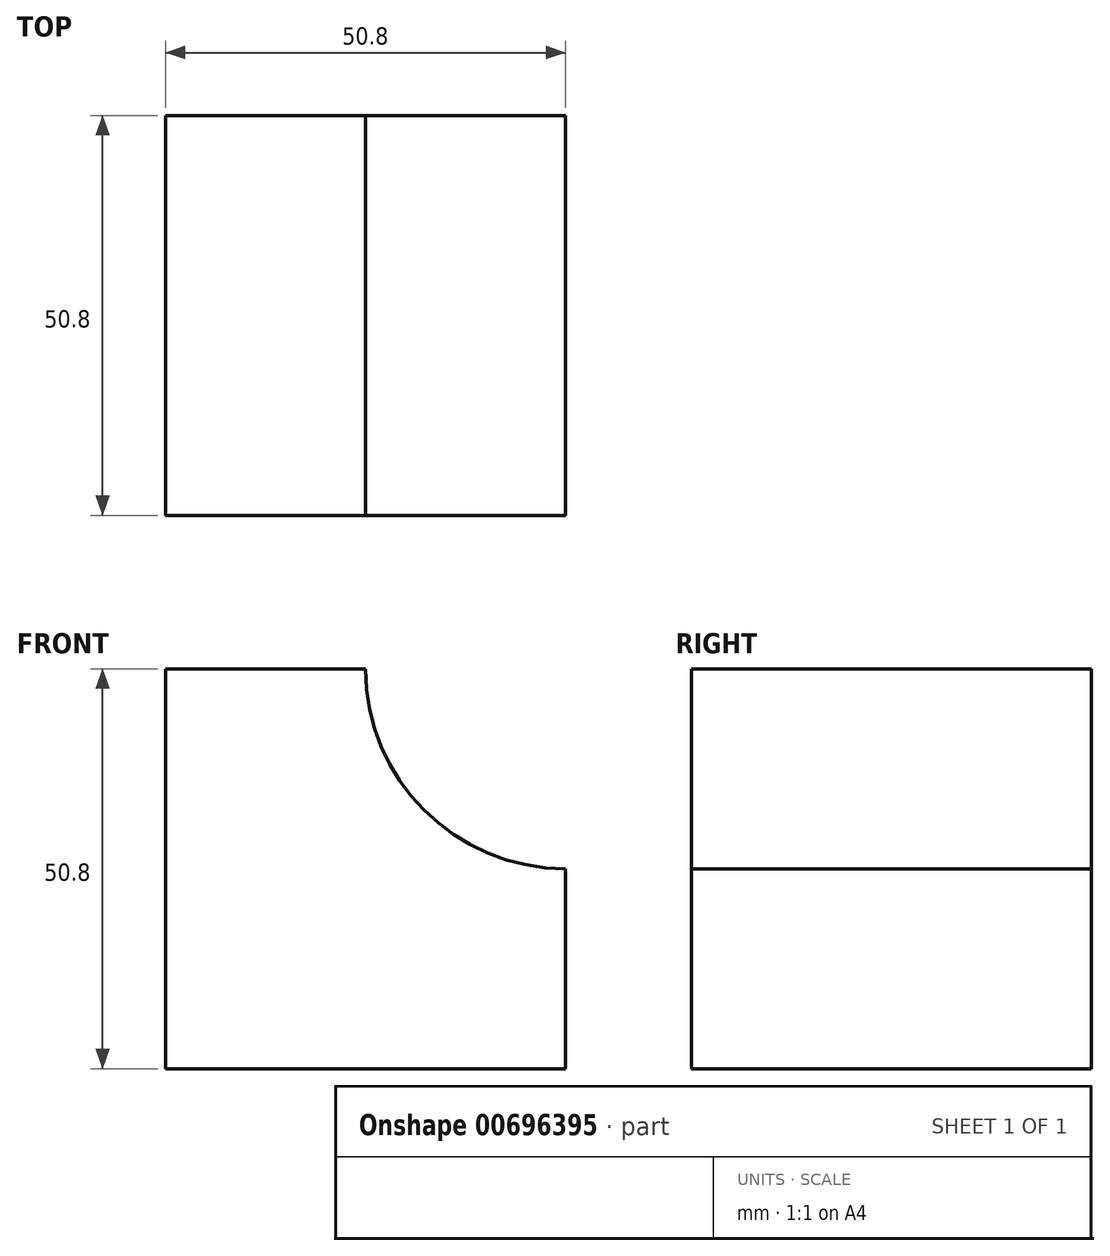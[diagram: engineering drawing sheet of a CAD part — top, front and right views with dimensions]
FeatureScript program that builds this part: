
annotation { "Feature Type Name" : "Feature", "Feature Type Description" : "" }
export const myFeature = defineFeature(function(context is Context, id is Id, definition is map)
    precondition{}
    {
        {
            var Q0;
            Q0=qCreatedBy(makeId("Front.planeOp"),FACE);
            var sketch = newSketch(context, id + "F0", { "sketchPlane" : qUnion([Q0])});
            skLineSegment(sketch, "E0", {"start": v(0, 0) * mm, "end": v(-50.8, 0) * mm});
            skLineSegment(sketch, "E1", {"start": v(-50.8, 0) * mm, "end": v(-50.8, 50.8) * mm});
            skLineSegment(sketch, "E2", {"start": v(0, 0) * mm, "end": v(0, 25.4) * mm});
            skLineSegment(sketch, "E3", {"start": v(-50.8, 50.8) * mm, "end": v(-25.4, 50.8) * mm});
            skArc(sketch, "E4", {"start": v(-25.4, 50.8) * mm, "mid": v(-17.96, 32.84) * mm, "end": v(0, 25.4) * mm});
            skSolve(sketch);
        }
        {
            var Q0;
            Q0=makeQuery(id+"F0.imprint","IMPRINT",FACE,{"disambiguationData":[TD([[makeQuery(id+"F0.imprint","IMPRINT",EDGE,{"derivedFrom":sQuery(id+"F0.wireOp",EDGE,"E0")}),-1.0]])]});
            extrude(context, id + "F1", {"entities" : qUnion([Q0]), "depth" : 50.8 * mm, "offsetDistance" : 25.4 * mm});
        }
    });
